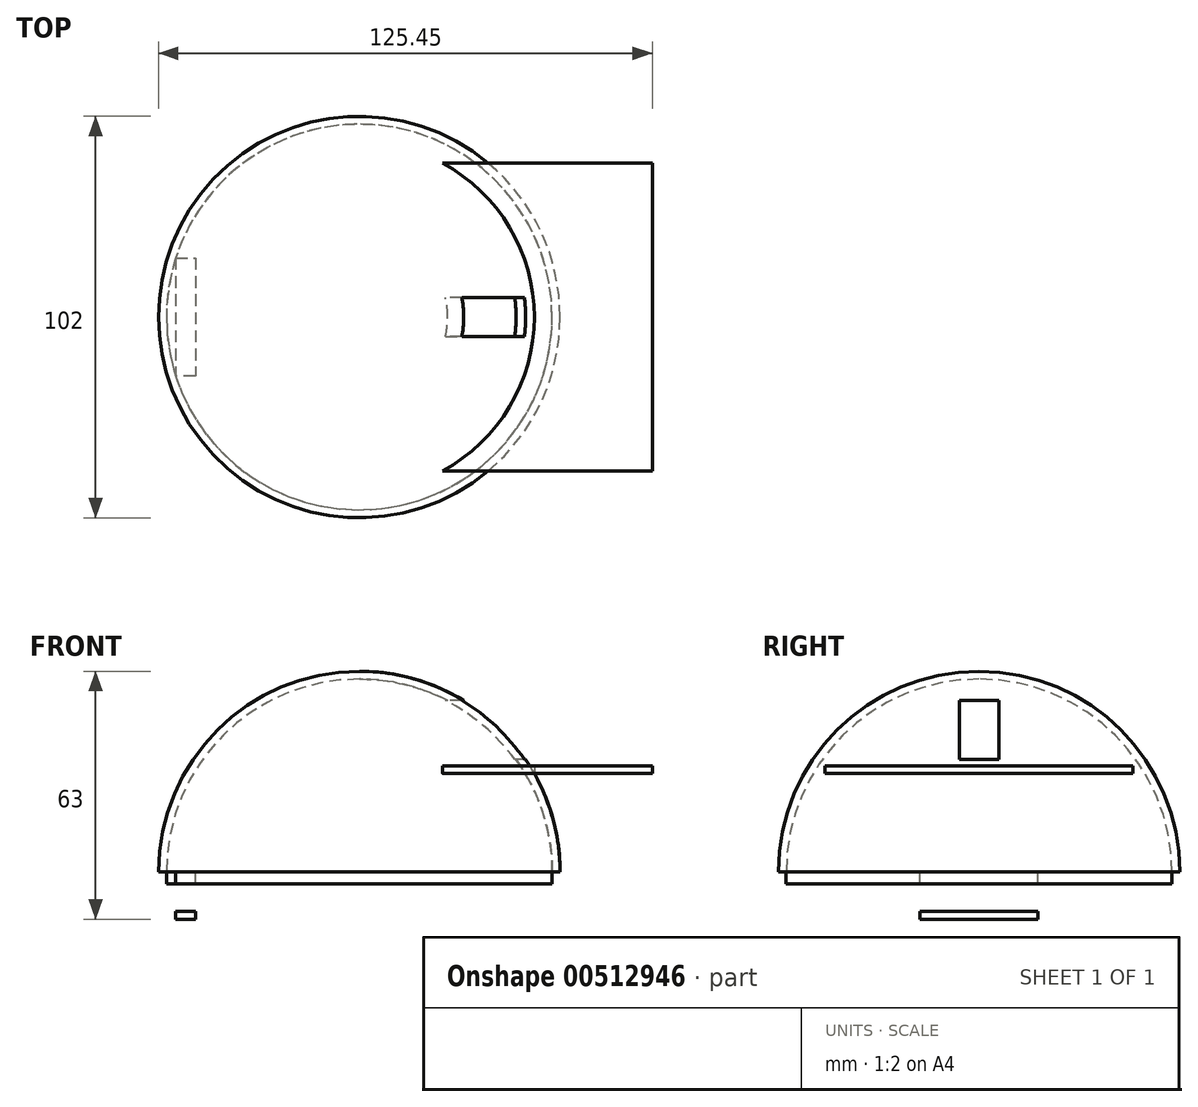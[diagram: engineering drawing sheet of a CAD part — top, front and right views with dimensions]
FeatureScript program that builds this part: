
annotation { "Feature Type Name" : "Feature", "Feature Type Description" : "" }
export const myFeature = defineFeature(function(context is Context, id is Id, definition is map)
    precondition{}
    {
        {
            var Q0;
            Q0=qCreatedBy(makeId("Front.planeOp"),FACE);
            var sketch = newSketch(context, id + "F0", { "sketchPlane" : qUnion([Q0])});
            skArc(sketch, "E0", {"start": v(51, 0) * mm, "mid": v(36.06, 36.06) * mm, "end": v(0, 51) * mm});
            skLineSegment(sketch, "E1", {"start": v(0, 51) * mm, "end": v(0, 0) * mm});
            skLineSegment(sketch, "E2", {"start": v(0, 0) * mm, "end": v(51, 0) * mm});
            skSolve(sketch);
        }
        {
            var Q0;
            Q0=makeQuery(id+"F0.imprint","IMPRINT",FACE,{"disambiguationData":[TD([[makeQuery(id+"F0.imprint","IMPRINT",EDGE,{"derivedFrom":sQuery(id+"F0.wireOp",EDGE,"E0")}),1.0]])]});
            var Q1;
            Q1=sQuery(id+"F0.wireOp",EDGE,"E1");
            revolve(context, id + "F1", {"entities" : qUnion([Q0]), "axis" : qUnion([Q1]), "revolveType" : RevolveType.FULL});
        }
        {
            var Q0;
            Q0=qCreatedBy(makeId("Front.planeOp"),FACE);
            var sketch = newSketch(context, id + "F2", { "sketchPlane" : qUnion([Q0])});
            skArc(sketch, "E3", {"start": v(49, 0) * mm, "mid": v(34.65, 34.65) * mm, "end": v(0, 49) * mm});
            skLineSegment(sketch, "E4", {"start": v(0, 49) * mm, "end": v(0, 0) * mm});
            skLineSegment(sketch, "E5", {"start": v(49, 0) * mm, "end": v(0, 0) * mm});
            skSolve(sketch);
        }
        {
            var Q0;
            Q0 = qSketchRegion(id + "F2", true);
            var Q1;
            Q1=sQuery(id+"F2.wireOp",EDGE,"E4");
            revolve(context, id + "F3", {"operationType" : NewBodyOperationType.REMOVE, "entities" : qUnion([Q0]), "axis" : qUnion([Q1]), "revolveType" : RevolveType.FULL, "oppositeDirection" : true});
        }
        {
            var Q0;
            Q0=qCreatedBy(makeId("Front.planeOp"),FACE);
            var sketch = newSketch(context, id + "F4", { "sketchPlane" : qUnion([Q0])});
            skLineSegment(sketch, "E6", {"start": v(0, 0) * mm, "end": v(0, 25) * mm});
            skArc(sketch, "E7", {"start": v(51, 0) * mm, "mid": v(36.06, 36.06) * mm, "end": v(0, 51) * mm});
            skLineSegment(sketch, "E8", {"start": v(44.45, 25) * mm, "end": v(74.45, 25) * mm});
            skLineSegment(sketch, "E9", {"start": v(0, 25) * mm, "end": v(44.45, 25) * mm});
            skLineSegment(sketch, "E10", {"start": v(44.45, 25) * mm, "end": v(44.45, 0) * mm});
            skSolve(sketch);
        }
        {
            var Q0;
            Q0=qCreatedBy(makeId("Top.planeOp"),FACE);
            cPlane(context, id + "F5", {"entities" : qUnion([Q0]), "cplaneType" : CPlaneType.OFFSET, "offset" : 25 * mm, "width" : 150 * mm, "height" : 150 * mm});
        }
        {
            var Q0;
            Q0=qCreatedBy(id+"F5.planeOp",FACE);
            var sketch = newSketch(context, id + "F6", { "sketchPlane" : qUnion([Q0])});
            skPoint(sketch, "E11.0", {"position": v(0, 0) * mm});
            skArc(sketch, "E12", {"start": v(0, -44.45) * mm, "mid": v(44.45, 0) * mm, "end": v(0, 44.45) * mm});
            skLineSegment(sketch, "E13", {"start": v(21.15, 39.1) * mm, "end": v(21.15, -39.1) * mm});
            skLineSegment(sketch, "E14", {"start": v(44.45, 0) * mm, "end": v(74.45, 0) * mm});
            skPoint(sketch, "E14.endSnap0", {"position": v(44.45, 0) * mm});
            skLineSegment(sketch, "E15", {"start": v(74.45, 0) * mm, "end": v(74.45, 39.1) * mm});
            skLineSegment(sketch, "E16", {"start": v(21.15, 39.1) * mm, "end": v(74.45, 39.1) * mm});
            skLineSegment(sketch, "E17", {"start": v(74.45, 0) * mm, "end": v(74.45, -39.1) * mm});
            skLineSegment(sketch, "E18", {"start": v(74.45, -39.1) * mm, "end": v(21.15, -39.1) * mm});
            skSolve(sketch);
        }
        {
            var Q0;
            {var subQ2=sQuery(id+"F6.wireOp",EDGE,"E14");Q0=makeQuery(id+"F6.imprint","IMPRINT",FACE,{"disambiguationData":[TD([[makeQuery(id+"F6.imprint","IMPRINT",EDGE,{"derivedFrom":subQ2}),-1.0]])]});}
            var Q1;
            {var subQ2=sQuery(id+"F6.wireOp",EDGE,"E14");Q1=makeQuery(id+"F6.imprint","IMPRINT",FACE,{"disambiguationData":[TD([[makeQuery(id+"F6.imprint","IMPRINT",EDGE,{"derivedFrom":subQ2}),1.0]])]});}
            extrude(context, id + "F7", {"entities" : qUnion([Q0, Q1]), "operationType" : NewBodyOperationType.ADD, "depth" : 2 * mm});
        }
        {
            var Q0;
            Q0=qCreatedBy(makeId("Front.planeOp"),FACE);
            var sketch = newSketch(context, id + "F8", { "sketchPlane" : qUnion([Q0])});
            skPoint(sketch, "E19.0", {"position": v(36.06, 36.06) * mm});
            skLineSegment(sketch, "E20", {"start": v(36.06, 36.06) * mm, "end": v(0, 36.06) * mm});
            skLineSegment(sketch, "E21", {"start": v(0, 36.06) * mm, "end": v(0, 43.56) * mm});
            skLineSegment(sketch, "E22", {"start": v(0, 36.06) * mm, "end": v(0, 28.56) * mm});
            skLineSegment(sketch, "E23", {"start": v(0, 43.56) * mm, "end": v(0, 28.56) * mm});
            skSolve(sketch);
        }
        {
            var Q0;
            Q0=qCreatedBy(makeId("Right.planeOp"),FACE);
            var sketch = newSketch(context, id + "F9", { "sketchPlane" : qUnion([Q0])});
            skPoint(sketch, "E24.0", {"position": v(0, 43.56) * mm});
            skPoint(sketch, "E25.0", {"position": v(0, 28.56) * mm});
            skPoint(sketch, "E26.0", {"position": v(0, 36.06) * mm});
            skLineSegment(sketch, "E27", {"start": v(0, 36.06) * mm, "end": v(-5, 36.06) * mm});
            skLineSegment(sketch, "E28", {"start": v(0, 36.06) * mm, "end": v(5, 36.06) * mm});
            skLineSegment(sketch, "E29", {"start": v(0, 43.56) * mm, "end": v(-5, 43.56) * mm});
            skLineSegment(sketch, "E30", {"start": v(-5, 43.56) * mm, "end": v(-5, 28.56) * mm});
            skLineSegment(sketch, "E31", {"start": v(-5, 28.56) * mm, "end": v(5, 28.56) * mm});
            skLineSegment(sketch, "E32", {"start": v(5, 28.56) * mm, "end": v(5, 43.56) * mm});
            skLineSegment(sketch, "E33", {"start": v(5, 43.56) * mm, "end": v(0, 43.56) * mm});
            skSolve(sketch);
        }
        {
            var Q0;
            Q0 = qSketchRegion(id + "F9", true);
            var Q1;
            Q1=sQuery(id+"F9.wireOp",EDGE,"E29");
            var Q2;
            Q2=sQuery(id+"F9.wireOp",EDGE,"E33");
            var Q3;
            Q3=sQuery(id+"F9.wireOp",EDGE,"E30");
            var Q4;
            Q4=sQuery(id+"F9.wireOp",EDGE,"E31");
            var Q5;
            Q5=sQuery(id+"F9.wireOp",EDGE,"E32");
            extrude(context, id + "F10", {"entities" : qUnion([Q0]), "operationType" : NewBodyOperationType.REMOVE, "surfaceEntities" : qUnion([Q1, Q2, Q3, Q4, Q5]), "depth" : 64.1 * mm});
        }
        {
            var Q0;
            Q0=qCreatedBy(makeId("Top.planeOp"),FACE);
            var sketch = newSketch(context, id + "F11", { "sketchPlane" : qUnion([Q0])});
            skLineSegment(sketch, "E34", {"start": v(0, 0) * mm, "end": v(-49, 0) * mm});
            skArc(sketch, "E35", {"start": v(0, 49) * mm, "mid": v(-49, 0) * mm, "end": v(0, -49) * mm});
            skLineSegment(sketch, "E36", {"start": v(-46.65, -15) * mm, "end": v(-46.65, 15) * mm});
            skLineSegment(sketch, "E37", {"start": v(-46.65, -15) * mm, "end": v(-41.65, -15) * mm});
            skLineSegment(sketch, "E38", {"start": v(-41.65, -15) * mm, "end": v(-41.65, 15) * mm});
            skLineSegment(sketch, "E39", {"start": v(-41.65, 15) * mm, "end": v(-46.65, 15) * mm});
            skArc(sketch, "E40", {"start": v(0, -49) * mm, "mid": v(49, 0) * mm, "end": v(0, 49) * mm});
            skSolve(sketch);
        }
        {
            var Q0;
            {var subQ1=sQuery(id+"F11.wireOp",EDGE,"E37");Q0=makeQuery(id+"F11.imprint","IMPRINT",FACE,{"disambiguationData":[TD([[makeQuery(id+"F11.imprint","IMPRINT",EDGE,{"derivedFrom":subQ1}),-1.0]])]});}
            var Q1;
            {var subQ0=sQuery(id+"F11.wireOp",EDGE,"E35");var subQ1=sQuery(id+"F11.wireOp",EDGE,"E34");var subQ2=makeQuery(id+"F11.imprint","INTERSECT",VERTEX,{"derivedFrom":[subQ1,subQ0]});Q1=makeQuery(id+"F11.imprint","IMPRINT",FACE,{"disambiguationData":[TD([[makeQuery(id+"F11.imprint","IMPRINT",EDGE,{"disambiguationData":[TD([[subQ2,1.0]])],"derivedFrom":subQ1}),1.0]])]});}
            var Q2;
            {var subQ0=sQuery(id+"F11.wireOp",EDGE,"E35");var subQ1=sQuery(id+"F11.wireOp",EDGE,"E34");var subQ2=makeQuery(id+"F11.imprint","INTERSECT",VERTEX,{"derivedFrom":[subQ1,subQ0]});Q2=makeQuery(id+"F11.imprint","IMPRINT",FACE,{"disambiguationData":[TD([[makeQuery(id+"F11.imprint","IMPRINT",EDGE,{"disambiguationData":[TD([[subQ2,1.0]])],"derivedFrom":subQ1}),-1.0]])]});}
            extrude(context, id + "F12", {"entities" : qUnion([Q0, Q1, Q2]), "oppositeDirection" : true, "depth" : 3 * mm});
        }
        {
            var Q0;
            {var subQ5=sQuery(id+"F11.wireOp",EDGE,"E37");Q0=makeQuery(id+"F11.imprint","IMPRINT",FACE,{"disambiguationData":[TD([[makeQuery(id+"F11.imprint","IMPRINT",EDGE,{"derivedFrom":subQ5}),1.0]])]});}
            var Q1;
            {var subQ5=sQuery(id+"F11.wireOp",EDGE,"E39");Q1=makeQuery(id+"F11.imprint","IMPRINT",FACE,{"disambiguationData":[TD([[makeQuery(id+"F11.imprint","IMPRINT",EDGE,{"derivedFrom":subQ5}),1.0]])]});}
            var Q2;
            Q2=sQuery(id+"F11.wireOp",EDGE,"E37");
            var Q3;
            Q3=sQuery(id+"F11.wireOp",EDGE,"E36");
            var Q4;
            Q4=sQuery(id+"F11.wireOp",EDGE,"E39");
            extrude(context, id + "F13", {"entities" : qUnion([Q0, Q1]), "bodyType" : ToolBodyType.SURFACE, "operationType" : NewBodyOperationType.INTERSECT, "surfaceEntities" : qUnion([Q2, Q3, Q4]), "oppositeDirection" : true, "depth" : 10 * mm});
        }
        {
            var Q0;
            Q0=qCreatedBy(makeId("Top.planeOp"),FACE);
            cPlane(context, id + "F14", {"entities" : qUnion([Q0]), "cplaneType" : CPlaneType.OFFSET, "offset" : 10 * mm, "oppositeDirection" : true, "width" : 150 * mm, "height" : 150 * mm});
        }
        {
            var Q0;
            Q0=qCreatedBy(id+"F14.planeOp",FACE);
            var sketch = newSketch(context, id + "F15", { "sketchPlane" : qUnion([Q0])});
            skPoint(sketch, "E41.0", {"position": v(-41.65, 15) * mm});
            skPoint(sketch, "E42.0", {"position": v(-46.65, 15) * mm});
            skPoint(sketch, "E43.0", {"position": v(-46.65, -15) * mm});
            skPoint(sketch, "E44.0", {"position": v(-41.65, -15) * mm});
            skLineSegment(sketch, "E45", {"start": v(-46.65, 15) * mm, "end": v(-46.65, -15) * mm});
            skLineSegment(sketch, "E46", {"start": v(-41.65, -15) * mm, "end": v(-46.65, -15) * mm});
            skLineSegment(sketch, "E47", {"start": v(-46.65, 15) * mm, "end": v(-41.65, 15) * mm});
            skLineSegment(sketch, "E48", {"start": v(-41.65, 15) * mm, "end": v(-41.65, -15) * mm});
            skSolve(sketch);
        }
        {
            var Q0;
            Q0 = qSketchRegion(id + "F15", true);
            var Q1;
            Q1 = qConstructionFilter(qBodyType(qCreatedBy(id + "F15" ,EDGE), BodyType.WIRE), ConstructionObject.NO);
            extrude(context, id + "F16", {"entities" : qUnion([Q0]), "surfaceEntities" : qUnion([Q1]), "oppositeDirection" : true, "depth" : 2 * mm});
        }
    });
